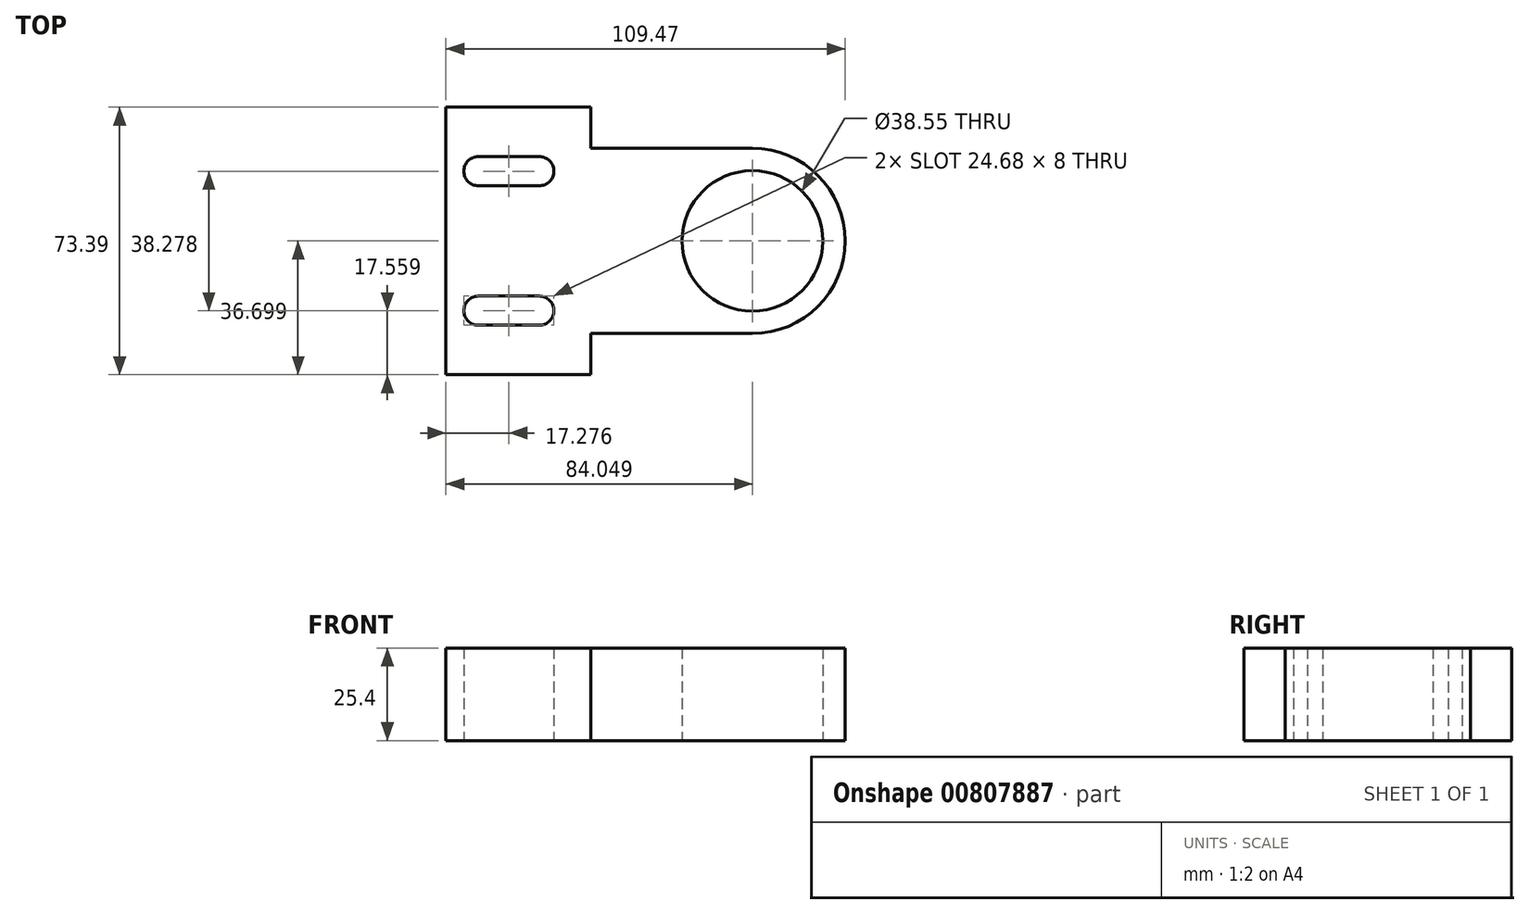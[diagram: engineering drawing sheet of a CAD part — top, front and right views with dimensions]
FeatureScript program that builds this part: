
annotation { "Feature Type Name" : "Feature", "Feature Type Description" : "" }
export const myFeature = defineFeature(function(context is Context, id is Id, definition is map)
    precondition{}
    {
        {
            var Q0;
            Q0=qCreatedBy(makeId("Top.planeOp"),FACE);
            var sketch = newSketch(context, id + "F0", { "sketchPlane" : qUnion([Q0])});
            skLineSegment(sketch, "E0", {"start": v(-50.52, 44.75) * mm, "end": v(-50.52, -28.64) * mm});
            skLineSegment(sketch, "E1", {"start": v(-50.52, -28.64) * mm, "end": v(-10.8, -28.64) * mm});
            skLineSegment(sketch, "E2", {"start": v(-50.52, 44.75) * mm, "end": v(-10.8, 44.75) * mm});
            skCircle(sketch, "E3", {"center": v(33.53, 8.06) * mm, "radius": 25.42 * mm});
            skPoint(sketch, "E3.centerSnap0", {"position": v(-50.52, 8.06) * mm});
            skCircle(sketch, "E4", {"center": v(33.53, 8.06) * mm, "radius": 19.28 * mm});
            skCircle(sketch, "E5", {"center": v(33.53, 8.06) * mm, "radius": 11.59 * mm});
            skLineSegment(sketch, "E6", {"start": v(33.53, 33.48) * mm, "end": v(-10.8, 33.48) * mm});
            skLineSegment(sketch, "E7", {"start": v(-10.8, 33.48) * mm, "end": v(-10.8, 44.75) * mm});
            skLineSegment(sketch, "E8", {"start": v(33.53, -17.37) * mm, "end": v(-10.8, -17.37) * mm});
            skLineSegment(sketch, "E9", {"start": v(-10.8, -17.37) * mm, "end": v(-10.8, -28.64) * mm});
            skArc(sketch, "E10", {"start": v(-41.59, 31.2) * mm, "mid": v(-45.59, 27.2) * mm, "end": v(-41.59, 23.2) * mm});
            skArc(sketch, "E11", {"start": v(-24.9, 23.2) * mm, "mid": v(-20.9, 27.2) * mm, "end": v(-24.9, 31.2) * mm});
            skLineSegment(sketch, "E12", {"start": v(-41.59, 31.2) * mm, "end": v(-24.9, 31.2) * mm});
            skLineSegment(sketch, "E13", {"start": v(-41.59, 23.2) * mm, "end": v(-24.9, 23.2) * mm});
            skLineSegment(sketch, "E14.MirrorCS", {"start": v(-41.59, -15.08) * mm, "end": v(-24.9, -15.08) * mm});
            skArc(sketch, "E15.MirrorCS", {"start": v(-41.59, -15.08) * mm, "mid": v(-45.59, -11.08) * mm, "end": v(-41.59, -7.08) * mm});
            skLineSegment(sketch, "E16.MirrorCS", {"start": v(-41.59, -7.08) * mm, "end": v(-24.9, -7.08) * mm});
            skArc(sketch, "E17.MirrorCS", {"start": v(-24.9, -7.08) * mm, "mid": v(-20.9, -11.08) * mm, "end": v(-24.9, -15.08) * mm});
            skSolve(sketch);
        }
        {
            var Q0;
            Q0 = qSketchRegion(id + "F0", true);
            extrude(context, id + "F1", {"entities" : qUnion([Q0]), "depth" : 25.4 * mm, "offsetDistance" : 25.4 * mm});
        }
    });
